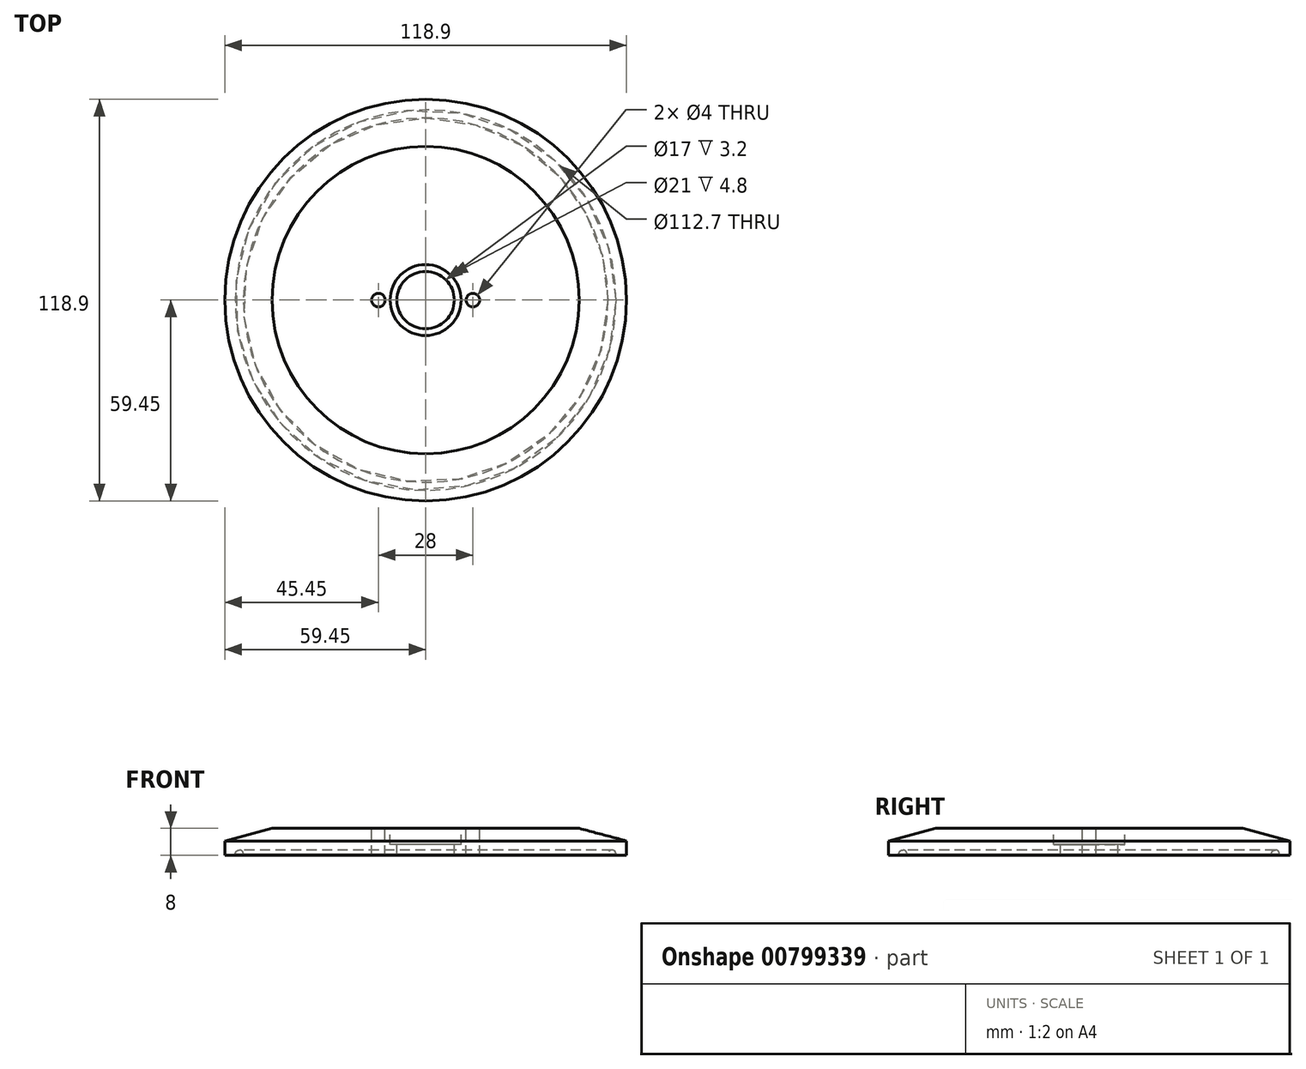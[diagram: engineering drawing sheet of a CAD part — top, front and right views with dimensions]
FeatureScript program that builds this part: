
annotation { "Feature Type Name" : "Feature", "Feature Type Description" : "" }
export const myFeature = defineFeature(function(context is Context, id is Id, definition is map)
    precondition{}
    {
        {
            var Q0;
            Q0=qCreatedBy(makeId("Front.planeOp"),FACE);
            var sketch = newSketch(context, id + "F0", { "sketchPlane" : qUnion([Q0])});
            skLineSegment(sketch, "E0", {"start": v(-8.5, 0) * mm, "end": v(-53.75, 0) * mm});
            skLineSegment(sketch, "E1", {"start": v(-59.45, 0) * mm, "end": v(-59.45, 4.3) * mm});
            skLineSegment(sketch, "E2", {"start": v(-45.5, 8) * mm, "end": v(-10.5, 8) * mm});
            skLineSegment(sketch, "E3", {"start": v(0, 8) * mm, "end": v(0, 0) * mm});
            skLineSegment(sketch, "E4", {"start": v(-10.5, 8) * mm, "end": v(-45.5, 8) * mm});
            skLineSegment(sketch, "E5", {"start": v(-45.5, 8) * mm, "end": v(-59.45, 4.3) * mm});
            skLineSegment(sketch, "E6", {"start": v(-8.5, 0) * mm, "end": v(-53.95, 0) * mm});
            skLineSegment(sketch, "E7", {"start": v(-55.15, 0) * mm, "end": v(-55.15, 0.4) * mm});
            skArc(sketch, "E8", {"start": v(-53.95, 0.36) * mm, "mid": v(-55.16, 1.6) * mm, "end": v(-56.35, 0.34) * mm});
            skLineSegment(sketch, "E9", {"start": v(-53.95, 0.44) * mm, "end": v(-53.95, 0.2) * mm});
            skLineSegment(sketch, "E10", {"start": v(-56.35, 0.46) * mm, "end": v(-56.35, 0.2) * mm});
            skLineSegment(sketch, "E11.trimOffspring", {"start": v(-56.55, 0) * mm, "end": v(-59.45, 0) * mm});
            skPoint(sketch, "E12.visualSharp", {"position": v(-56.35, 0) * mm});
            skArc(sketch, "E12.filletArc", {"start": v(-56.55, 0) * mm, "mid": v(-56.4, 0.06) * mm, "end": v(-56.35, 0.2) * mm});
            skPoint(sketch, "E13.visualSharp", {"position": v(-53.95, 0) * mm});
            skArc(sketch, "E13.filletArc", {"start": v(-53.95, 0.2) * mm, "mid": v(-53.9, 0.06) * mm, "end": v(-53.75, 0) * mm});
            skLineSegment(sketch, "E14.top", {"start": v(-8.5, 3.2) * mm, "end": v(-10.5, 3.2) * mm});
            skLineSegment(sketch, "E14.left", {"start": v(0, 8) * mm, "end": v(0, 3.2) * mm});
            skLineSegment(sketch, "E14.right", {"start": v(-10.5, 8) * mm, "end": v(-10.5, 3.2) * mm});
            skLineSegment(sketch, "E15", {"start": v(-8.5, 3.2) * mm, "end": v(-8.5, 0) * mm});
            skLineSegment(sketch, "E16", {"start": v(0, 8) * mm, "end": v(-14, 8) * mm});
            skLineSegment(sketch, "E17", {"start": v(-14, 8) * mm, "end": v(-14, 0) * mm});
            skLineSegment(sketch, "E18.left", {"start": v(-16, -1.05) * mm, "end": v(-16, 8) * mm});
            skLineSegment(sketch, "E18.right", {"start": v(-12, -1.05) * mm, "end": v(-12, 8) * mm});
            skPoint(sketch, "E18.middle", {"position": v(-14, 8) * mm});
            skPoint(sketch, "E18.top.end.orphan", {"position": v(-12, 17.05) * mm});
            skPoint(sketch, "E18.top.start.orphan", {"position": v(-16, 17.05) * mm});
            skSolve(sketch);
        }
        {
            var Q0;
            Q0=makeQuery(id+"F0.imprint","IMPRINT",FACE,{"disambiguationData":[TD([[makeQuery(id+"F0.imprint","IMPRINT",EDGE,{"derivedFrom":sQuery(id+"F0.wireOp",EDGE,"E1")}),-1.0]])]});
            var Q1;
            {var subQ0=sQuery(id+"F0.wireOp",EDGE,"E17");Q1=makeQuery(id+"F0.imprint","IMPRINT",FACE,{"disambiguationData":[TD([[makeQuery(id+"F0.imprint","IMPRINT",EDGE,{"derivedFrom":subQ0}),1.0]])]});}
            var Q2;
            {var subQ3=sQuery(id+"F0.wireOp",EDGE,"E17");Q2=makeQuery(id+"F0.imprint","IMPRINT",FACE,{"disambiguationData":[TD([[makeQuery(id+"F0.imprint","IMPRINT",EDGE,{"derivedFrom":subQ3}),-1.0]])]});}
            var Q3;
            Q3=makeQuery(id+"F0.imprint","IMPRINT",FACE,{"disambiguationData":[TD([[makeQuery(id+"F0.imprint","IMPRINT",EDGE,{"derivedFrom":sQuery(id+"F0.wireOp",EDGE,"E14.top")}),1.0]])]});
            var Q4;
            Q4=sQuery(id+"F0.wireOp",EDGE,"E14.left");
            revolve(context, id + "F1", {"surfaceOperationType" : NewSurfaceOperationType.NEW, "entities" : qUnion([Q0, Q1, Q2, Q3]), "axis" : qUnion([Q4]), "revolveType" : RevolveType.FULL});
        }
        {
            var Q0;
            Q0=makeQuery(id+"F1.opRevolve","SWEPT_FACE",FACE,{"disambiguationData":[OSD([sQuery(id+"F0.wireOp",EDGE,"E2")])]});
            var sketch = newSketch(context, id + "F2", { "sketchPlane" : qUnion([Q0])});
            skCircle(sketch, "E19", {"center": v(0, 0) * mm, "radius": 14 * mm});
            skCircle(sketch, "E20", {"center": v(14, 0) * mm, "radius": 2 * mm});
            skCircle(sketch, "E21", {"center": v(-14, 0) * mm, "radius": 2 * mm});
            skSolve(sketch);
        }
        {
            var Q0;
            {var subQ0=sQuery(id+"F2.wireOp",EDGE,"E21");var subQ1=sQuery(id+"F2.wireOp",EDGE,"E19");var subQ2=makeQuery(id+"F2.imprint","INTERSECT",VERTEX,{"disambiguationData":[OD(0.0)],"derivedFrom":[subQ1,subQ0]});Q0=makeQuery(id+"F2.imprint","IMPRINT",FACE,{"disambiguationData":[TD([[makeQuery(id+"F2.imprint","IMPRINT",EDGE,{"disambiguationData":[TD([[subQ2,-1.0]])],"derivedFrom":subQ1}),-1.0]])]});}
            var Q1;
            {var subQ0=sQuery(id+"F2.wireOp",EDGE,"E21");var subQ1=sQuery(id+"F2.wireOp",EDGE,"E19");var subQ2=makeQuery(id+"F2.imprint","INTERSECT",VERTEX,{"disambiguationData":[OD(0.0)],"derivedFrom":[subQ1,subQ0]});Q1=makeQuery(id+"F2.imprint","IMPRINT",FACE,{"disambiguationData":[TD([[makeQuery(id+"F2.imprint","IMPRINT",EDGE,{"disambiguationData":[TD([[subQ2,-1.0]])],"derivedFrom":subQ1}),1.0]])]});}
            var Q2;
            {var subQ0=sQuery(id+"F2.wireOp",EDGE,"E20");var subQ1=sQuery(id+"F2.wireOp",EDGE,"E19");var subQ2=makeQuery(id+"F2.imprint","INTERSECT",VERTEX,{"disambiguationData":[OD(0.0)],"derivedFrom":[subQ1,subQ0]});Q2=makeQuery(id+"F2.imprint","IMPRINT",FACE,{"disambiguationData":[TD([[makeQuery(id+"F2.imprint","IMPRINT",EDGE,{"disambiguationData":[TD([[subQ2,1.0]])],"derivedFrom":subQ1}),1.0]])]});}
            var Q3;
            {var subQ0=sQuery(id+"F2.wireOp",EDGE,"E20");var subQ1=sQuery(id+"F2.wireOp",EDGE,"E19");var subQ2=makeQuery(id+"F2.imprint","INTERSECT",VERTEX,{"disambiguationData":[OD(0.0)],"derivedFrom":[subQ1,subQ0]});Q3=makeQuery(id+"F2.imprint","IMPRINT",FACE,{"disambiguationData":[TD([[makeQuery(id+"F2.imprint","IMPRINT",EDGE,{"disambiguationData":[TD([[subQ2,1.0]])],"derivedFrom":subQ1}),-1.0]])]});}
            extrude(context, id + "F3", {"entities" : qUnion([Q0, Q1, Q2, Q3]), "operationType" : NewBodyOperationType.REMOVE, "oppositeDirection" : true, "depth" : 25 * mm, "offsetDistance" : 25 * mm});
        }
    });
